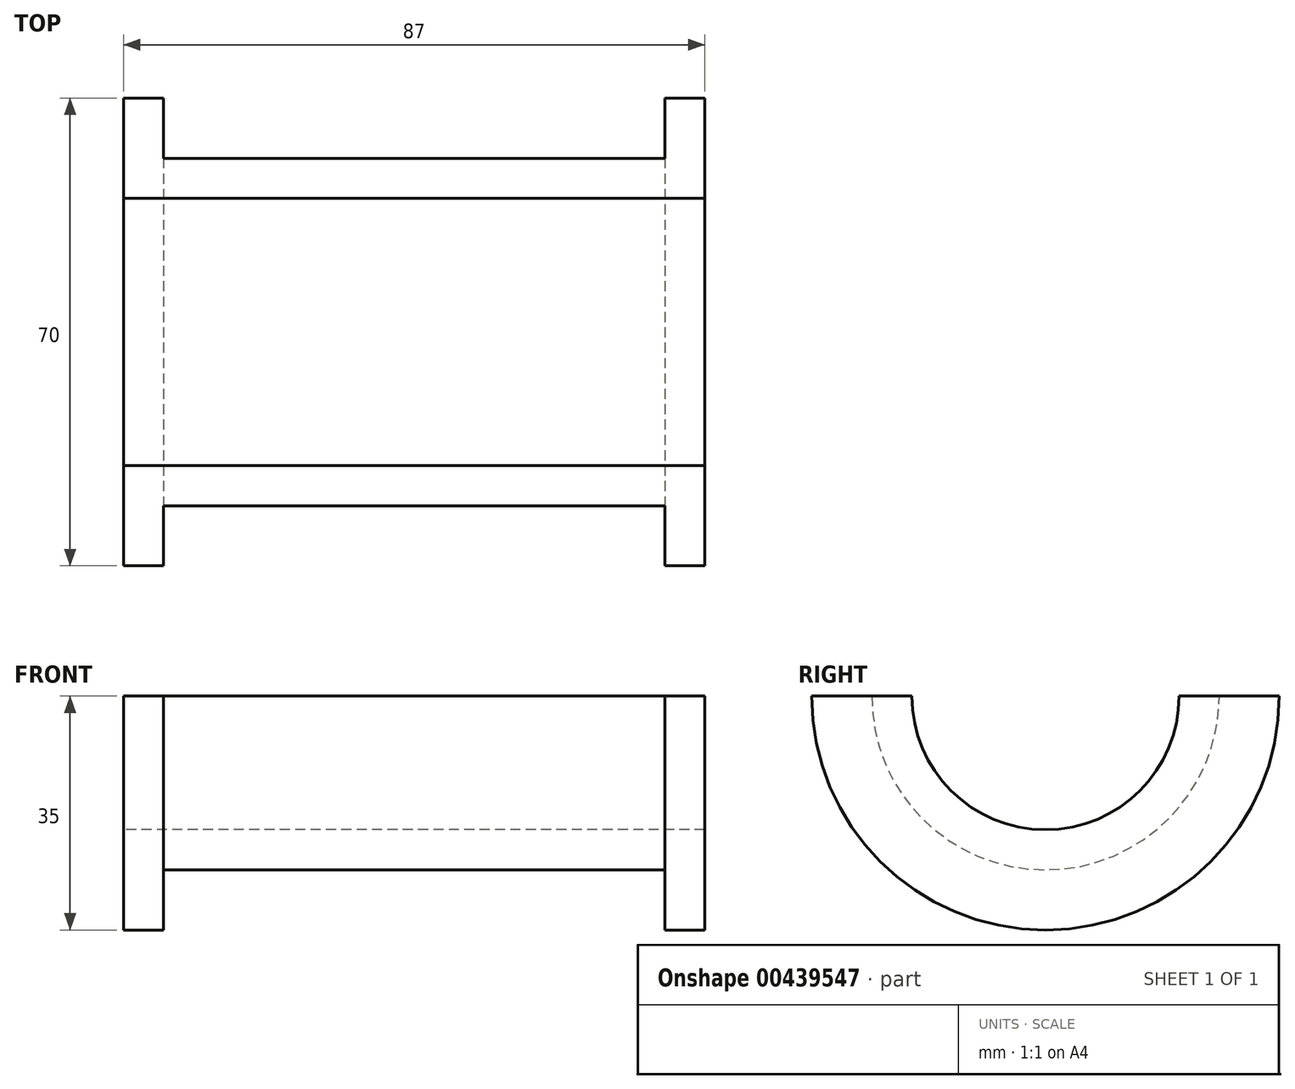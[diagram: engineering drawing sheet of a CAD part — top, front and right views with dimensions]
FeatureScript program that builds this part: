
annotation { "Feature Type Name" : "Feature", "Feature Type Description" : "" }
export const myFeature = defineFeature(function(context is Context, id is Id, definition is map)
    precondition{}
    {
        {
            var Q0;
            Q0=qCreatedBy(makeId("Top.planeOp"),FACE);
            var sketch = newSketch(context, id + "F0", { "sketchPlane" : qUnion([Q0])});
            skLineSegment(sketch, "E0.bottom", {"start": v(-43.5, -20) * mm, "end": v(43.5, -20) * mm});
            skLineSegment(sketch, "E0.top", {"start": v(-43.5, -26) * mm, "end": v(43.5, -26) * mm});
            skLineSegment(sketch, "E0.left", {"start": v(-43.5, -20) * mm, "end": v(-43.5, -26) * mm});
            skLineSegment(sketch, "E0.right", {"start": v(43.5, -20) * mm, "end": v(43.5, -26) * mm});
            skLineSegment(sketch, "E1.bottom", {"start": v(43.5, -20) * mm, "end": v(37.5, -20) * mm});
            skLineSegment(sketch, "E1.top", {"start": v(43.5, -35) * mm, "end": v(37.5, -35) * mm});
            skLineSegment(sketch, "E1.left", {"start": v(43.5, -20) * mm, "end": v(43.5, -35) * mm});
            skLineSegment(sketch, "E1.right", {"start": v(37.5, -20) * mm, "end": v(37.5, -35) * mm});
            skLineSegment(sketch, "E2.bottom", {"start": v(-43.5, -20) * mm, "end": v(-37.5, -20) * mm});
            skLineSegment(sketch, "E2.top", {"start": v(-43.5, -35) * mm, "end": v(-37.5, -35) * mm});
            skLineSegment(sketch, "E2.left", {"start": v(-43.5, -20) * mm, "end": v(-43.5, -35) * mm});
            skLineSegment(sketch, "E2.right", {"start": v(-37.5, -20) * mm, "end": v(-37.5, -35) * mm});
            skLineSegment(sketch, "E3", {"start": v(0, 30.33) * mm, "end": v(0, -30.33) * mm, "construction": true});
            skLineSegment(sketch, "E4", {"start": v(-71.79, 0) * mm, "end": v(77.72, 0) * mm, "construction": true});
            skSolve(sketch);
        }
        {
            var Q0;
            {var subQ5=sQuery(id+"F0.wireOp",EDGE,"E2.top");Q0=makeQuery(id+"F0.imprint","IMPRINT",FACE,{"disambiguationData":[TD([[makeQuery(id+"F0.imprint","IMPRINT",EDGE,{"derivedFrom":subQ5}),1.0]])]});}
            var Q1;
            {var subQ5=sQuery(id+"F0.wireOp",EDGE,"E2.bottom");Q1=makeQuery(id+"F0.imprint","IMPRINT",FACE,{"disambiguationData":[TD([[makeQuery(id+"F0.imprint","IMPRINT",EDGE,{"derivedFrom":subQ5}),-1.0]])]});}
            var Q2;
            {var subQ0=sQuery(id+"F0.wireOp",EDGE,"E0.bottom");Q2=makeQuery(id+"F0.imprint","IMPRINT",FACE,{"disambiguationData":[TD([[makeQuery(id+"F0.imprint","IMPRINT",EDGE,{"derivedFrom":subQ0}),-1.0]])]});}
            var Q3;
            {var subQ5=sQuery(id+"F0.wireOp",EDGE,"E1.bottom");Q3=makeQuery(id+"F0.imprint","IMPRINT",FACE,{"disambiguationData":[TD([[makeQuery(id+"F0.imprint","IMPRINT",EDGE,{"derivedFrom":subQ5}),1.0]])]});}
            var Q4;
            {var subQ5=sQuery(id+"F0.wireOp",EDGE,"E1.top");Q4=makeQuery(id+"F0.imprint","IMPRINT",FACE,{"disambiguationData":[TD([[makeQuery(id+"F0.imprint","IMPRINT",EDGE,{"derivedFrom":subQ5}),-1.0]])]});}
            var Q5;
            Q5=sQuery(id+"F0.wireOp",EDGE,"E4");
            revolve(context, id + "F1", {"entities" : qUnion([Q0, Q1, Q2, Q3, Q4]), "axis" : qUnion([Q5]), "revolveType" : RevolveType.ONE_DIRECTION, "angle" : 180 * degree});
        }
    });
